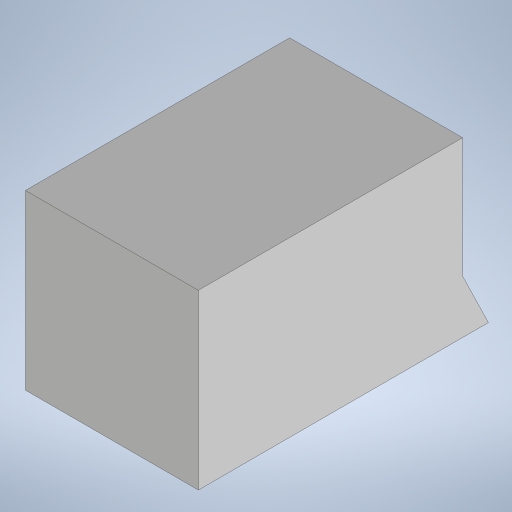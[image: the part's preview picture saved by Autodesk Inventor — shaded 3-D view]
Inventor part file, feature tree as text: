
AUTODESK INVENTOR PART (.ipt)
format: ipt  version: 2024 (Build 280153000, 153)  size: 10,711,552 bytes
history: native  units: mm
features: other x6, sketch x6, extrude x5, plane x2
ambient origin geometry x8: Origin, YZ Plane, XZ Plane, XY Plane, X Axis, Y Axis, Z Axis, Center Point
bodies: Body1 (feature_tree)
feature tree (19):
  other  "M.ipt"
  plane  "Plano de trabajo1"
  extrude  "Extrusión1"  [1 undecoded]
  other  "Combinar1"
  sketch  "Boceto3"  dims[d2=550.0mm d3=520.0mm]
  sketch  "Boceto4"  dims[d4=550.0mm d5=0.0mm d6=129.8482mm]
  plane  "Plano de trabajo2"
  sketch  "Boceto5"  dims[d17=180.0mm d18=180.0mm]
  extrude  "Extrusión2"  Depth=520.0mm
  extrude  "Extrusión3"  Depth=129.8482mm
  extrude  "Extrusión4"  Depth=180.0mm
  extrude  "Extrusión5"  Depth=180.0mm
  other  "Sólido1::M.ipt"
  other  "OperaciónIdentificador1"
  sketch  "Boceto1"  dims[d0=25.0mm d1=-365.0mm]
  other  "Sólido2"
  sketch  "Boceto6"  dims[d22=326.0mm d23=180.0mm]
  sketch  "Boceto7"  dims[d24=180.0mm d25=180.0mm d26=10.0mm d27=0.0mm d28=1000.0mm d29=0.0mm d30=30.0mm d31=30.0mm d32=16.0mm d33=16.0mm d34=0.0mm d35=30.0mm d36=30.0mm d37=16.0mm d38=16.0mm d39=0.0mm d14=0.5mm d15=0.872665mm d16=0.5mm d19=0.5mm d20=0.872665mm d21=0.5mm]
  other  "Sólido1"
note: 1 required parameter value undecoded (feature->parameter linkage not recoverable at this tier; creation-order binding heuristic only, values carry confidence <= 0.55)
